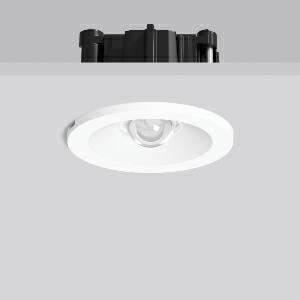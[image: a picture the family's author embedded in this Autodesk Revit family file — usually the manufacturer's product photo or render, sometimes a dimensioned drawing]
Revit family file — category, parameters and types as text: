
# Revit family: turia_l_672413_002_e05b
name_source: partatom
category: Lighting Fixtures
units: mm (PartAtom-declared; Revit-internal decimal feet)

## family parameters
Cut with Voids When Loaded = No
Host = Face
Light Source = No
Part Type = Normal
Room Calculation Point = No
Round Connector Dimension = Use Diameter
Shared = No

## types (1)
- TURIA L (1 x LED Modul 765, 270 lm, 6500)
    Apparent Load = 4 VA
    CIE Flux Codes = 16 58 99 100 100
    Color Rendering = 70
    Color Temperature = 6500
    Default Elevation = 1800 mm
    Description = Series: TURIA L
Round emergency luminaire for escape route lighting. Housing: die-cast aluminium. Bezel ring: plastic. With plastic lenses for area lighting. Self-contained system with automatic self-test. With enclosed separate ceiling mounting ring also suitable for ceiling cut-outs of Ø 68 mm. 
Colour: white
Diameter: 62 mm
Height: 3 mm
Cut-out diameter: 54-68 mm
Recess height: 76-162 mm
Luminaire: recess height: 42 mm
Weight: 550 g
Operating mode: non-maintained power mode
Duration time: 8 h
Lamp: LED
Socket: without socket
Colour temperature: 6500K
Colour rendering index (CRI): 70
System power: 4.2 W
Rated luminous flux: 270 lm
Luminous flux, emergency: 130 lm
System power, emergency: -
Control gear: Regulated power supply
Protection class: II
Type of protection: IP 20
    Height = 0 mm  [stored 0 ft]
    Lamp = 1 x LED Modul 765
    Lamp Light Flux = 270 lm
    Lamp count = 1
    Length = 62 mm  [stored 0.203412 ft]
    Lifetime = 50000 h
    Luminous efficacy = 64 lm/W
    Manufacturer = RZB
    ModVariant = No
    Model = 672413.002
    Mounting Place = Ceiling
    Mounting Type = Recessed
    Number of Poles = 1
    OnlyDefault = Yes
    Power Factor = 1
    Product Name = TURIA L
    Product group = Recessed ceiling luminaires
    ProductGroupID = 405
    Protection Class = Protection class II
    Protection Degree = IP 20
    RLX_Detail_Level = 1
    RLX_Emergency_Light_Flux = 130 lm
    RLX_Emergency_Type = 3
    RLX_Emergency_Type_DB = Yes
    RlxData = <blob elided: 36217 chars, md5=fa3ed219>
    Socket = socket
    Standby Power = 0 W
    System Light Flux = 270 lm
    System Power = 4 W
    Type Comments = Product without accessories
    Type Image = 672412.002.jpg
    URL = http://relux.com
    VarID = ---
    Voltage = 230 V
    Voltage Range = 220-240 V
    Weight = 0.00 kg
    Width = 0 mm  [stored 0 ft]

note: [stored X ft] marks values corroborated as IEEE doubles in the binary element streams (Revit-internal decimal feet)

## geometry (parser evidence)
native form markers: Blend x4, Sweep x11
no freeform markers — native parametric forms only
